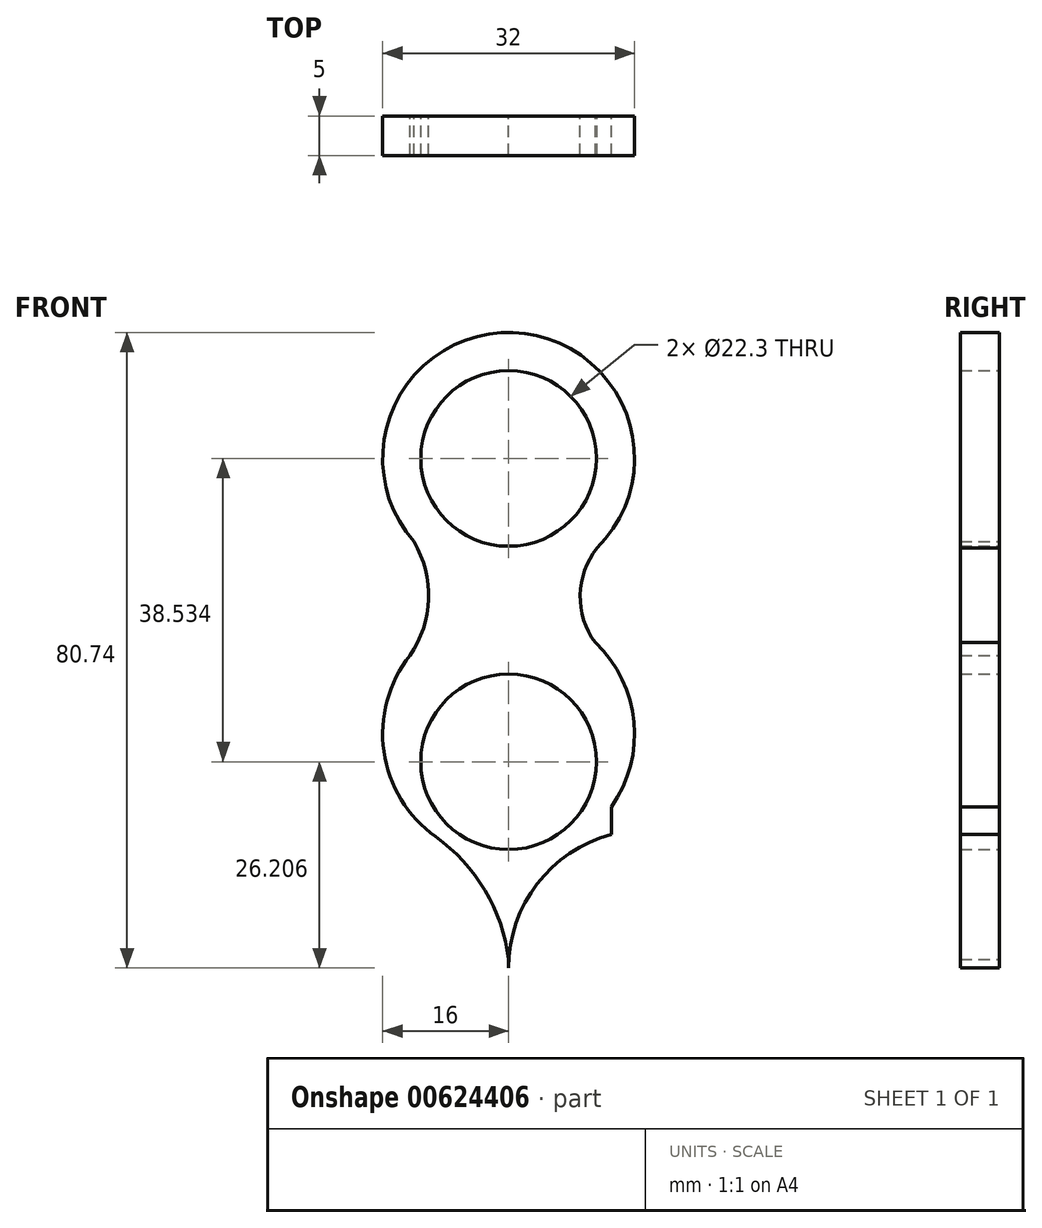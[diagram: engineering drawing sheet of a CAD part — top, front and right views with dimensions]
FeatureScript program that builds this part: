
annotation { "Feature Type Name" : "Feature", "Feature Type Description" : "" }
export const myFeature = defineFeature(function(context is Context, id is Id, definition is map)
    precondition{}
    {
        {
            var Q0;
            Q0=qCreatedBy(makeId("Front.planeOp"),FACE);
            var sketch = newSketch(context, id + "F0", { "sketchPlane" : qUnion([Q0])});
            skCircle(sketch, "E0", {"center": v(0, 0) * mm, "radius": 16 * mm});
            skCircle(sketch, "E1", {"center": v(0, -35) * mm, "radius": 16 * mm});
            skPoint(sketch, "E2.endSnap0", {"position": v(-5.04, -65.17) * mm});
            skArc(sketch, "E3", {"start": v(12.22, -10.32) * mm, "mid": v(9.09, -17.7) * mm, "end": v(12.46, -24.96) * mm});
            skArc(sketch, "E4", {"start": v(-13.17, -25.92) * mm, "mid": v(-10.2, -18.43) * mm, "end": v(-12.01, -10.57) * mm});
            skLineSegment(sketch, "E5", {"start": v(0, -51) * mm, "end": v(0, -64.74) * mm});
            skArc(sketch, "E6", {"start": v(13.04, -47.79) * mm, "mid": v(3.64, -54.04) * mm, "end": v(0, -64.74) * mm});
            skLineSegment(sketch, "E7", {"start": v(13.04, -47.79) * mm, "end": v(13.04, -44.27) * mm});
            skArc(sketch, "E8", {"start": v(0, -69.25) * mm, "mid": v(-1.74, -57.33) * mm, "end": v(-9.35, -47.98) * mm});
            skSolve(sketch);
        }
        {
            var Q0;
            Q0 = qSketchRegion(id + "F0", true);
            extrude(context, id + "F1", {"entities" : qUnion([Q0]), "depth" : 5 * mm, "offsetDistance" : 25 * mm});
        }
        {
            var Q0;
            Q0=qCreatedBy(makeId("Front.planeOp"),FACE);
            var sketch = newSketch(context, id + "F2", { "sketchPlane" : qUnion([Q0])});
            skCircle(sketch, "E9", {"center": v(0, 0) * mm, "radius": 11.15 * mm});
            skCircle(sketch, "E10", {"center": v(0, -38.53) * mm, "radius": 11.15 * mm});
            skSolve(sketch);
        }
        {
            var Q0;
            Q0 = qSketchRegion(id + "F2", true);
            extrude(context, id + "F3", {"entities" : qUnion([Q0]), "operationType" : NewBodyOperationType.REMOVE, "endBound" : BoundingType.UP_TO_NEXT, "depth" : 25 * mm, "offsetDistance" : 25 * mm});
        }
        {
            var Q0;
            Q0=qCreatedBy(makeId("Top.planeOp"),FACE);
            var sketch = newSketch(context, id + "F4", { "sketchPlane" : qUnion([Q0])});
            skLineSegment(sketch, "E11", {"start": v(0, 0) * mm, "end": v(0, 30.04) * mm});
            skSolve(sketch);
        }
        {
            var Q0;
            Q0=makeQuery(id+"F1.opExtrude","SWEPT_BODY",BODY,{"disambiguationData":[OSD([sQuery(id+"F0.wireOp",EDGE,"E0"),sQuery(id+"F0.wireOp",EDGE,"E1"),sQuery(id+"F0.wireOp",EDGE,"eiaZb4mF-GUBm-Zrki-jpCW-hvlTksbNiSvp"),sQuery(id+"F0.wireOp",EDGE,"W8JVVHej-hKCc-Mwun-CbA6-SytXtQ0Ulk2M")])]});
            var Q1;
            Q1=sQuery(id+"F4.wireOp",EDGE,"E11");
            circularPattern(context, id + "F5", {"entities" : qUnion([Q0]), "axis" : qUnion([Q1]), "angle" : 360 * degree, "instanceCount" : 3, "equalSpace" : true});
        }
        {
            var Q0;
            Q0=makeQuery(id+"F5.opPattern","COPY",BODY,{"derivedFrom":makeQuery(id+"F1.opExtrude","SWEPT_BODY",BODY,{"disambiguationData":[OSD([sQuery(id+"F0.wireOp",EDGE,"E0"),sQuery(id+"F0.wireOp",EDGE,"E1"),sQuery(id+"F0.wireOp",EDGE,"E3"),sQuery(id+"F0.wireOp",EDGE,"E4")])]}),"instanceName":"2"});
            var Q1;
            Q1=makeQuery(id+"F5.opPattern","COPY",BODY,{"derivedFrom":makeQuery(id+"F1.opExtrude","SWEPT_BODY",BODY,{"disambiguationData":[OSD([sQuery(id+"F0.wireOp",EDGE,"E0"),sQuery(id+"F0.wireOp",EDGE,"E1"),sQuery(id+"F0.wireOp",EDGE,"E3"),sQuery(id+"F0.wireOp",EDGE,"E4")])]}),"instanceName":"1"});
            deleteBodies(context, id + "F6", {"entities" : qUnion([Q0, Q1])});
        }
    });
